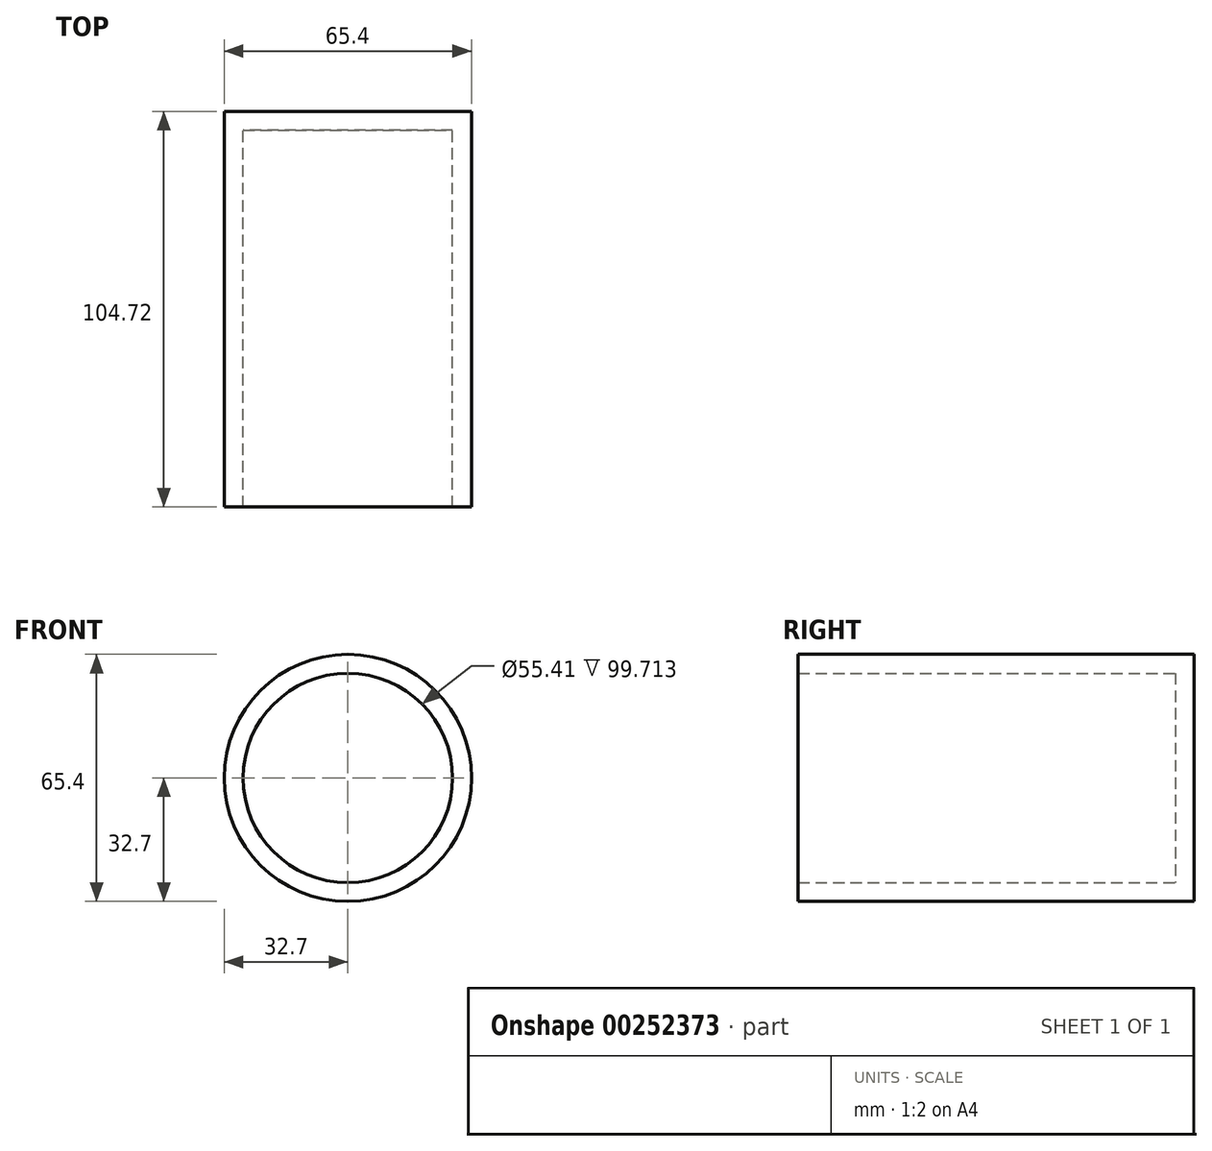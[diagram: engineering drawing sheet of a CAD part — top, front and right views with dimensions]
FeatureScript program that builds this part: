
annotation { "Feature Type Name" : "Feature", "Feature Type Description" : "" }
export const myFeature = defineFeature(function(context is Context, id is Id, definition is map)
    precondition{}
    {
        {
            var Q0;
            Q0=qCreatedBy(makeId("Top.planeOp"),FACE);
            var sketch = newSketch(context, id + "F0", { "sketchPlane" : qUnion([Q0])});
            skLineSegment(sketch, "E0.bottom", {"start": v(32.7, 52.36) * mm, "end": v(-32.7, 52.36) * mm});
            skLineSegment(sketch, "E0.top", {"start": v(32.7, -52.36) * mm, "end": v(-32.7, -52.36) * mm});
            skLineSegment(sketch, "E0.left", {"start": v(32.7, 52.36) * mm, "end": v(32.7, -52.36) * mm});
            skLineSegment(sketch, "E0.right", {"start": v(-32.7, 52.36) * mm, "end": v(-32.7, -52.36) * mm});
            skPoint(sketch, "E0.middle", {"position": v(0, 0) * mm});
            skLineSegment(sketch, "E1", {"start": v(0, 52.36) * mm, "end": v(0, -52.36) * mm});
            skSolve(sketch);
        }
        {
            var Q0;
            {var subQ0=sQuery(id+"F0.wireOp",EDGE,"E0.right");Q0=makeQuery(id+"F0.imprint","IMPRINT",FACE,{"disambiguationData":[TD([[makeQuery(id+"F0.imprint","IMPRINT",EDGE,{"derivedFrom":subQ0}),1.0]])]});}
            var Q1;
            Q1=sQuery(id+"F0.wireOp",EDGE,"E1");
            revolve(context, id + "F1", {"entities" : qUnion([Q0]), "axis" : qUnion([Q1]), "revolveType" : RevolveType.FULL});
        }
        {
            var Q0;
            Q0=makeQuery(id+"F1.opRevolve","SWEPT_FACE",FACE,{"disambiguationData":[OSD([sQuery(id+"F0.wireOp",EDGE,"E0.top")])]});
            shell(context, id + "F2", {"entities" : qUnion([Q0]), "thickness" : 5 * mm});
        }
    });
